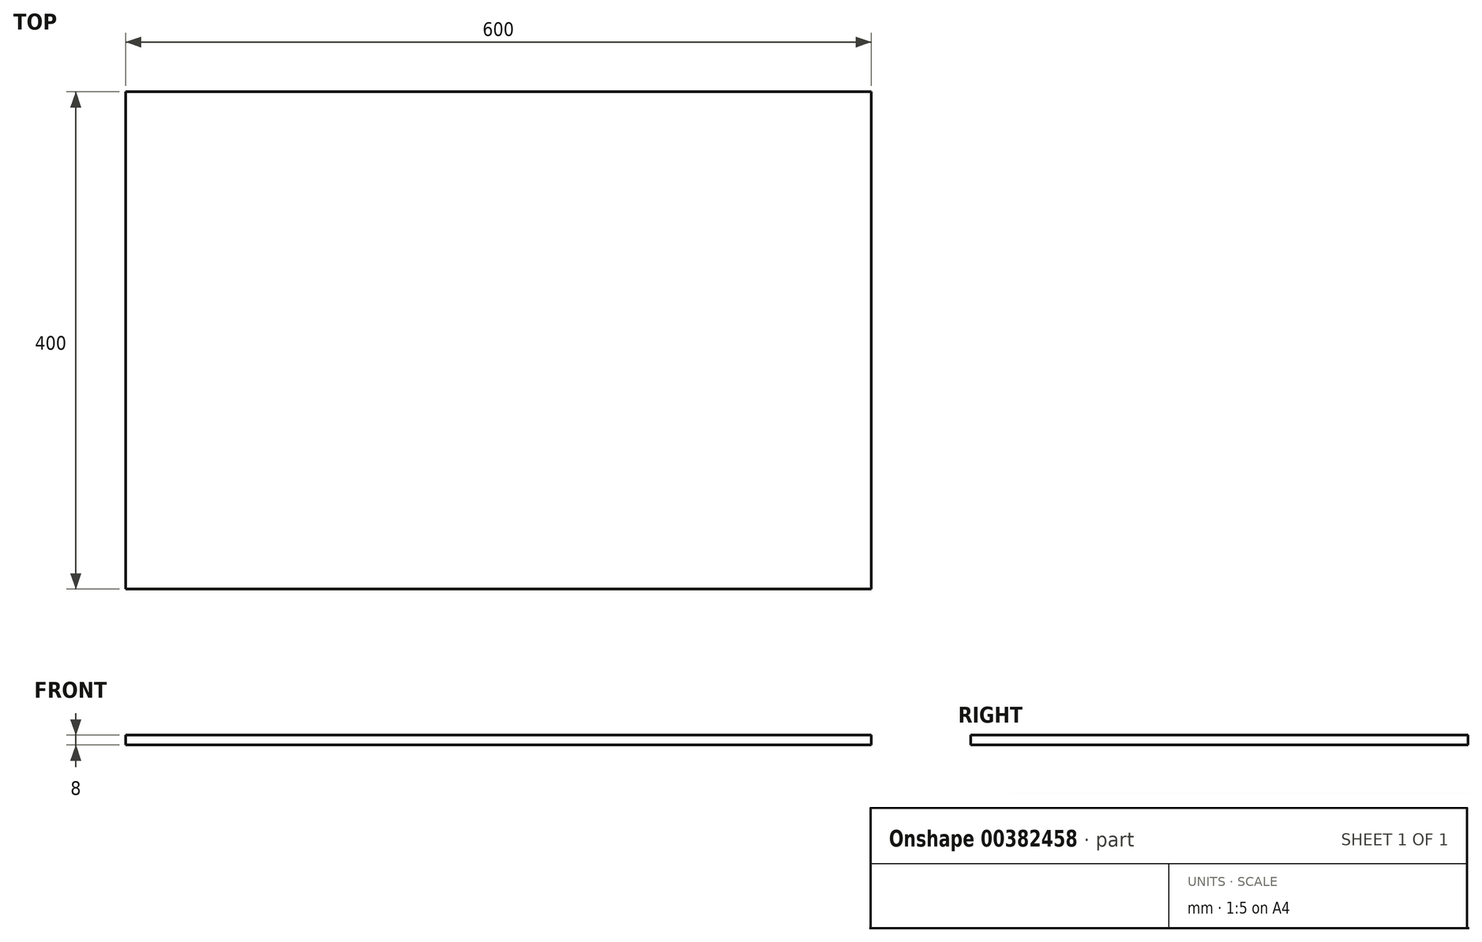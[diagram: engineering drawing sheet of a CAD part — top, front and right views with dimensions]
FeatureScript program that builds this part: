
annotation { "Feature Type Name" : "Feature", "Feature Type Description" : "" }
export const myFeature = defineFeature(function(context is Context, id is Id, definition is map)
    precondition{}
    {
        {
            var Q0;
            Q0=qCreatedBy(makeId("Top.planeOp"),FACE);
            var sketch = newSketch(context, id + "F0", { "sketchPlane" : qUnion([Q0])});
            skLineSegment(sketch, "E0.bottom", {"start": v(-300, 200) * mm, "end": v(300, 200) * mm});
            skLineSegment(sketch, "E0.top", {"start": v(-300, -200) * mm, "end": v(300, -200) * mm});
            skLineSegment(sketch, "E0.left", {"start": v(-300, 200) * mm, "end": v(-300, -200) * mm});
            skLineSegment(sketch, "E0.right", {"start": v(300, 200) * mm, "end": v(300, -200) * mm});
            skPoint(sketch, "E0.middle", {"position": v(0, 0) * mm});
            skSolve(sketch);
        }
        {
            var Q0;
            Q0=makeQuery(id+"F0.imprint","IMPRINT",FACE,{"disambiguationData":[TD([[makeQuery(id+"F0.imprint","IMPRINT",EDGE,{"derivedFrom":sQuery(id+"F0.wireOp",EDGE,"E0.bottom")}),-1.0]])]});
            extrude(context, id + "F1", {"entities" : qUnion([Q0]), "endBound" : BoundingType.SYMMETRIC, "depth" : 8 * mm});
        }
    });
